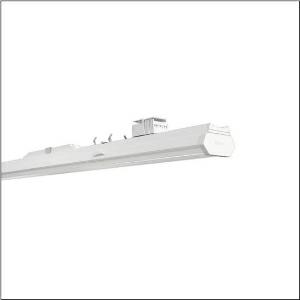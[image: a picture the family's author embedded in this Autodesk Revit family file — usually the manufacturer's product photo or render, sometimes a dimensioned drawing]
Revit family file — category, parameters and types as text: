
# Revit family: licross_r__11_protected_mo_51td12cn49xg_1fdf
name_source: partatom
category: Lighting Fixtures
units: mm (PartAtom-declared; Revit-internal decimal feet)

## family parameters
Cut with Voids When Loaded = No
Host = Face
Light Source = No
Part Type = Normal
Room Calculation Point = No
Round Connector Dimension = Use Diameter
Shared = No

## types (1)
- --- (1 x LED, 9070 lm, 49.4 W, 4000K)
    Apparent Load = 49 VA
    CIE Flux Codes = 73 92 98 99 100
    Color Rendering = 80
    Color Temperature = 4000K
    Default Elevation = 1800 mm
    Description = Licross® 11 Protected MO, luminaire insert, of sheet steel, galvanised, coil coated, white, length: 1.500mm, width: 90mm, height: 101mm, LED rated luminous flux: 9.070lm, light colour: 840, control gear: ON/OFF Multilumen, CLOi, with plug, 3-pole, with phase selection, mains connection: 220..240V, AC, 50/60Hz, start of lifetime: 49W, end of service life: 55W, halogen-free wiring, primary light control with lens, of plastic, primary optical cover: cover, of PMMA, light emission: direct distribution, primary light characteristic: symmetric, protection rating (complete): IP54, insulation class (complete): insulation class I (protective earthing), certification: CE, ENEC, VDE, UKCA, protection symbol: D if used in an environment with non-conductive dust loads with corresponding accessories, impact resistance: IK06, permissible ambient temperature for indoor applications: -35..+40°C, corresponds to IFS (International Featured Standards) requirements for safety and quality in the food industry, reducing of maximum allowable ambient temperature of 5°C with ceiling mounting, LABS conformity tested according to VDMA 24364:2018-05, packaging unit: 1 piece
    Height = 92 mm
    Lamp = 1 x LED
    Lamp Light Flux = 9070 lm
    Lamp Power = 49.4 W
    Lamp count = 1
    Length = 1500 mm
    Luminous efficacy = 184 lm/W
    Manufacturer = Siteco
    ModVariant = No
    Model = 51TD12CN49XG
    Mounting Place = Ceiling
    Mounting Type = Pendant
    Number of Poles = 1
    OnlyDefault = Yes
    Power Factor = 1
    Product Name = Licross® 11 Protected MO
    Product group = luminaire insert
    ProductGroupID = 902
    Protection Class = Protection class I
    Protection Degree = IP 54
    RLX_Detail_Level = 1
    RLX_Emergency_Light_Flux = 0 lm
    RLX_Emergency_Type = 0
    RLX_Emergency_Type_DB = No
    RlxData = <blob elided: 22065 chars, md5=bdac9b3c>
    Socket = socket
    Standby Power = 0 W
    System Light Flux = 9070 lm
    System Power = 49 W
    Type Comments = factory setting: luminous flux: 100 % | (A | C | E) | 113 mA
    Type Image = l_1256145.jpg
    URL = http://relux.com
    VarID = @adj_085888
    Voltage = 0 V
    Weight = 0.00 kg
    Width = 88 mm

## geometry (parser evidence)
native form markers: Blend x4, Sweep x10
no freeform markers — native parametric forms only
